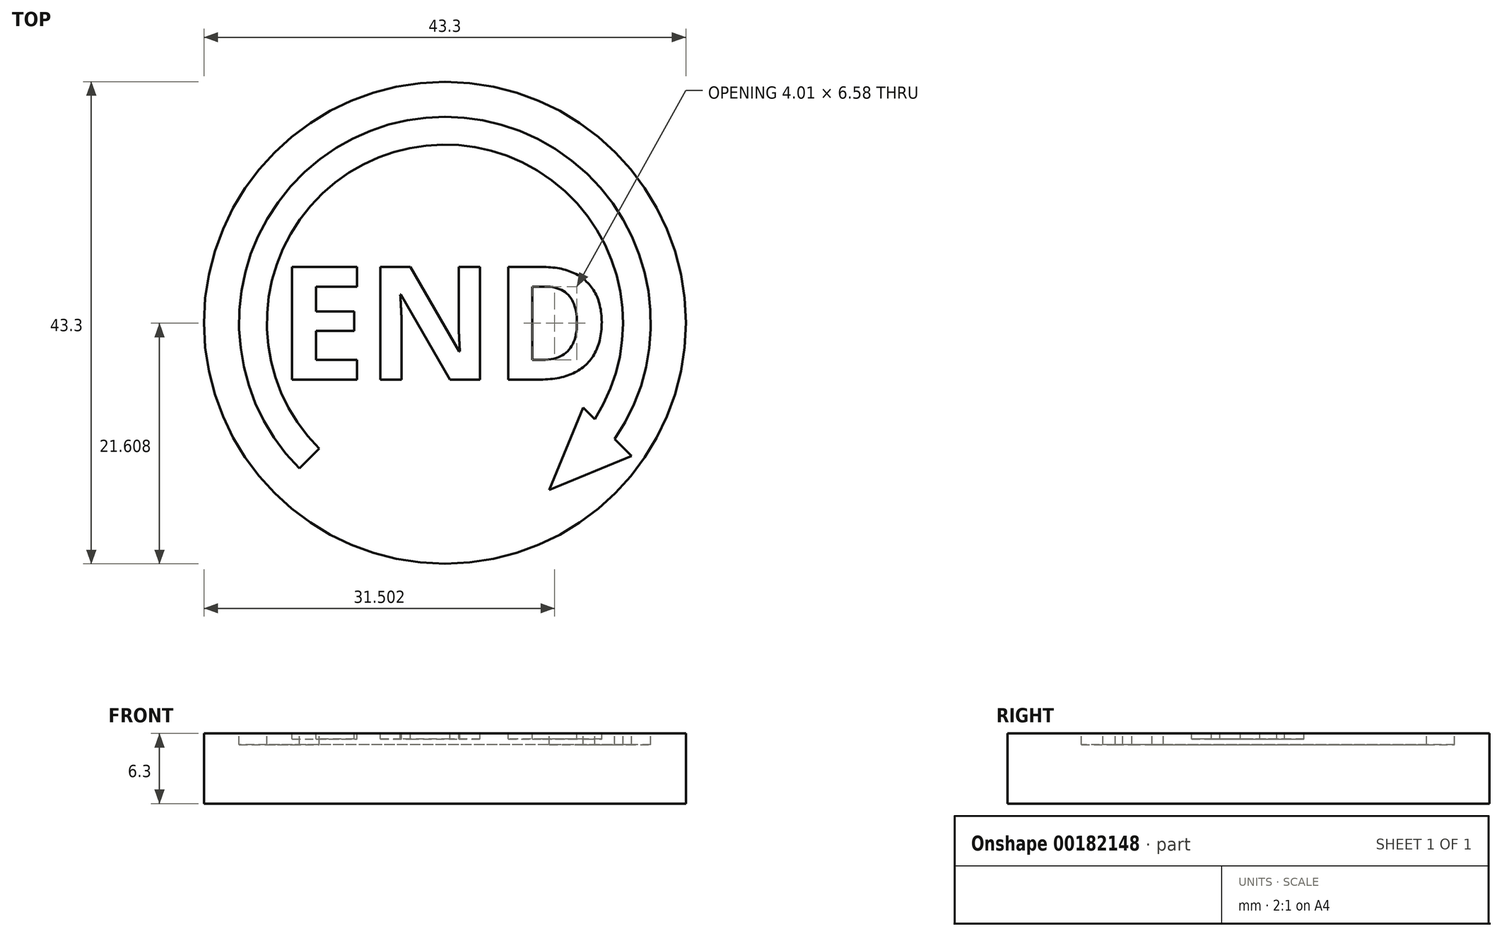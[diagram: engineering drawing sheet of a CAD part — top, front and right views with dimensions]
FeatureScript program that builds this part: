
annotation { "Feature Type Name" : "Feature", "Feature Type Description" : "" }
export const myFeature = defineFeature(function(context is Context, id is Id, definition is map)
    precondition{}
    {
        {
            var Q0;
            Q0=qCreatedBy(makeId("Top.planeOp"),FACE);
            var sketch = newSketch(context, id + "F0", { "sketchPlane" : qUnion([Q0])});
            skCircle(sketch, "E0", {"center": v(0, 0) * mm, "radius": 22.25 * mm, "construction": true});
            skCircle(sketch, "E1.0", {"center": v(0, 0) * mm, "radius": 21.65 * mm});
            skSolve(sketch);
        }
        {
            var Q0;
            Q0=makeQuery(id+"F0.imprint","IMPRINT",FACE,{"disambiguationData":[TD([[makeQuery(id+"F0.imprint","IMPRINT",EDGE,{"derivedFrom":sQuery(id+"F0.wireOp",EDGE,"E1.0")}),1.0]])]});
            extrude(context, id + "F1", {"entities" : qUnion([Q0]), "depth" : 6.3 * mm});
        }
        {
            var Q0;
            Q0=makeQuery(id+"F1.opExtrude","CAP_FACE",FACE,{"disambiguationData":[OSD([sQuery(id+"F0.wireOp",EDGE,"E1.0")])],"isStart":false});
            var sketch = newSketch(context, id + "F2", { "sketchPlane" : qUnion([Q0])});
            skArc(sketch, "E2", {"start": v(11.31, -11.31) * mm, "mid": v(0, 16) * mm, "end": v(-11.31, -11.31) * mm});
            skLineSegment(sketch, "E3", {"start": v(0, -18.65) * mm, "end": v(0, -21.65) * mm, "construction": true});
            skArc(sketch, "E4", {"start": v(13.08, -13.08) * mm, "mid": v(0, 18.5) * mm, "end": v(-13.08, -13.08) * mm});
            skLineSegment(sketch, "E5", {"start": v(0, 0) * mm, "end": v(11.31, -11.31) * mm, "construction": true});
            skLineSegment(sketch, "E6.MirrorCS", {"start": v(0, 0) * mm, "end": v(-11.31, -11.31) * mm, "construction": true});
            skLineSegment(sketch, "E7", {"start": v(-11.31, -11.31) * mm, "end": v(-13.08, -13.08) * mm});
            skLineSegment(sketch, "E8.MirrorCS", {"start": v(11.31, -11.31) * mm, "end": v(13.08, -13.08) * mm, "construction": true});
            skLineSegment(sketch, "E9", {"start": v(12.43, -7.63) * mm, "end": v(9.37, -15.03) * mm});
            skLineSegment(sketch, "E10", {"start": v(9.37, -15.03) * mm, "end": v(16.76, -11.96) * mm});
            skLineSegment(sketch, "E11", {"start": v(12.43, -7.63) * mm, "end": v(13.45, -8.66) * mm});
            skLineSegment(sketch, "E12", {"start": v(16.76, -11.96) * mm, "end": v(15.26, -10.46) * mm});
            skLineSegment(sketch, "E13", {"start": v(13.45, -8.66) * mm, "end": v(15.26, -10.46) * mm, "construction": true});
            skLineSegment(sketch, "E14", {"start": v(12.2, -12.2) * mm, "end": v(9.37, -15.03) * mm, "construction": true});
            skSolve(sketch);
        }
        {
            var Q0;
            Q0 = qSketchRegion(id + "F2", true);
            extrude(context, id + "F3", {"entities" : qUnion([Q0]), "operationType" : NewBodyOperationType.REMOVE, "oppositeDirection" : true, "depth" : 1 * mm});
        }
        {
            var Q0;
            Q0=makeQuery(id+"F1.opExtrude","CAP_FACE",FACE,{"disambiguationData":[OSD([sQuery(id+"F0.wireOp",EDGE,"E1.0")])],"isStart":false});
            var sketch = newSketch(context, id + "F4", { "sketchPlane" : qUnion([Q0])});
            skText(sketch, "E15", { "text": "END", "fontName": "OpenSans-Bold.ttf"});
            const initialGuessF4  = {"E15": [-0.015, -0.0051, 1, 0, 0.01019]};
            skSetInitialGuess(sketch, initialGuessF4);
            skSolve(sketch);
        }
        {
            var Q0;
            Q0 = qSketchRegion(id + "F4", true);
            extrude(context, id + "F5", {"entities" : qUnion([Q0]), "operationType" : NewBodyOperationType.REMOVE, "oppositeDirection" : true, "depth" : .5 * mm});
        }
        {
            var Q0;
            {var subQ0=sQuery(id+"F0.wireOp",EDGE,"E1.0");Q0=makeQuery(id+"F5.boolean.opBoolean","SPLIT",FACE,{"disambiguationData":[TD([makeQuery(id+"F1.opExtrude","SWEPT_FACE",FACE,{"disambiguationData":[OSD([subQ0])]})])],"derivedFrom":makeQuery(id+"F1.opExtrude","CAP_FACE",FACE,{"disambiguationData":[OSD([subQ0])],"isStart":false})});}
            var sketch = newSketch(context, id + "F6", { "sketchPlane" : qUnion([Q0])});
            skLineSegment(sketch, "E16.0", {"start": v(-11.31, -11.31) * mm, "end": v(-13.08, -13.08) * mm});
            skArc(sketch, "E17.0", {"start": v(15.26, -10.46) * mm, "mid": v(-1.7, 18.42) * mm, "end": v(-13.08, -13.08) * mm});
            skArc(sketch, "E18.0", {"start": v(13.45, -8.66) * mm, "mid": v(-1.7, 15.9) * mm, "end": v(-11.31, -11.31) * mm});
            skLineSegment(sketch, "E19.0", {"start": v(12.43, -7.63) * mm, "end": v(13.45, -8.66) * mm});
            skLineSegment(sketch, "E20.0", {"start": v(12.43, -7.63) * mm, "end": v(9.37, -15.03) * mm});
            skLineSegment(sketch, "E21.0", {"start": v(9.37, -15.03) * mm, "end": v(16.76, -11.96) * mm});
            skLineSegment(sketch, "E22.0", {"start": v(16.76, -11.96) * mm, "end": v(15.26, -10.46) * mm});
            skSolve(sketch);
        }
        {
            var Q0;
            Q0=makeQuery(id+"F6.imprint","IMPRINT",FACE,{"disambiguationData":[TD([[makeQuery(id+"F6.imprint","IMPRINT",EDGE,{"derivedFrom":sQuery(id+"F6.wireOp",EDGE,"E16.0")}),-1.0]])]});
            extrude(context, id + "F7", {"entities" : qUnion([Q0]), "endBound" : BoundingType.UP_TO_NEXT, "oppositeDirection" : true, "depth" : 25 * mm, "offsetDistance" : 25 * mm});
        }
        {
            var Q0;
            Q0=makeQuery(id+"F4.imprint","IMPRINT",FACE,{"disambiguationData":[TD([[makeQuery(id+"F4.imprint","IMPRINT",EDGE,{"derivedFrom":sQuery(id+"F4.wireOp",EDGE,"E15.sketch_text.stroke-0")}),-1.0]])]});
            var Q1;
            Q1=makeQuery(id+"F4.imprint","IMPRINT",FACE,{"disambiguationData":[TD([[makeQuery(id+"F4.imprint","IMPRINT",EDGE,{"derivedFrom":sQuery(id+"F4.wireOp",EDGE,"E15.sketch_text.stroke-12")}),-1.0]])]});
            var Q2;
            Q2=makeQuery(id+"F4.imprint","IMPRINT",FACE,{"disambiguationData":[TD([[makeQuery(id+"F4.imprint","IMPRINT",EDGE,{"derivedFrom":sQuery(id+"F4.wireOp",EDGE,"E15.sketch_text.stroke-26")}),-1.0]])]});
            extrude(context, id + "F8", {"entities" : qUnion([Q0, Q1, Q2]), "endBound" : BoundingType.UP_TO_NEXT, "oppositeDirection" : true, "depth" : 25 * mm, "offsetDistance" : 25 * mm});
        }
    });
